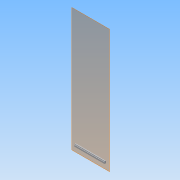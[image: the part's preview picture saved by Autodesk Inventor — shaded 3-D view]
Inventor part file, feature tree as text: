
AUTODESK INVENTOR PART (.ipt)
format: ipt  version: 2013 (Build 170138000, 138)  size: 77,312 bytes
history: native  units: in
note: dims shown in document units (in); Inventor stores cm internally (conversion verified against a paired STEP export)
features: extrude x2, sketch x2, plane x1
ambient origin geometry x8: Origin, YZ Plane, XZ Plane, XY Plane, X Axis, Y Axis, Z Axis, Center Point
bodies: Solid1 (feature_tree)
feature tree (5):
  plane  "Work Plane1"
  extrude  "Extrusion1"  Depth=1.5in
  extrude  "Extrusion2"  Depth=0.5in
  sketch  "Sketch1"  dims[d0=21.0in d1=1.5in]
  sketch  "Sketch2"  dims[d2=1.0in d3=0.0in d4=0.5in d5=0.3332in d6=0.0in]
